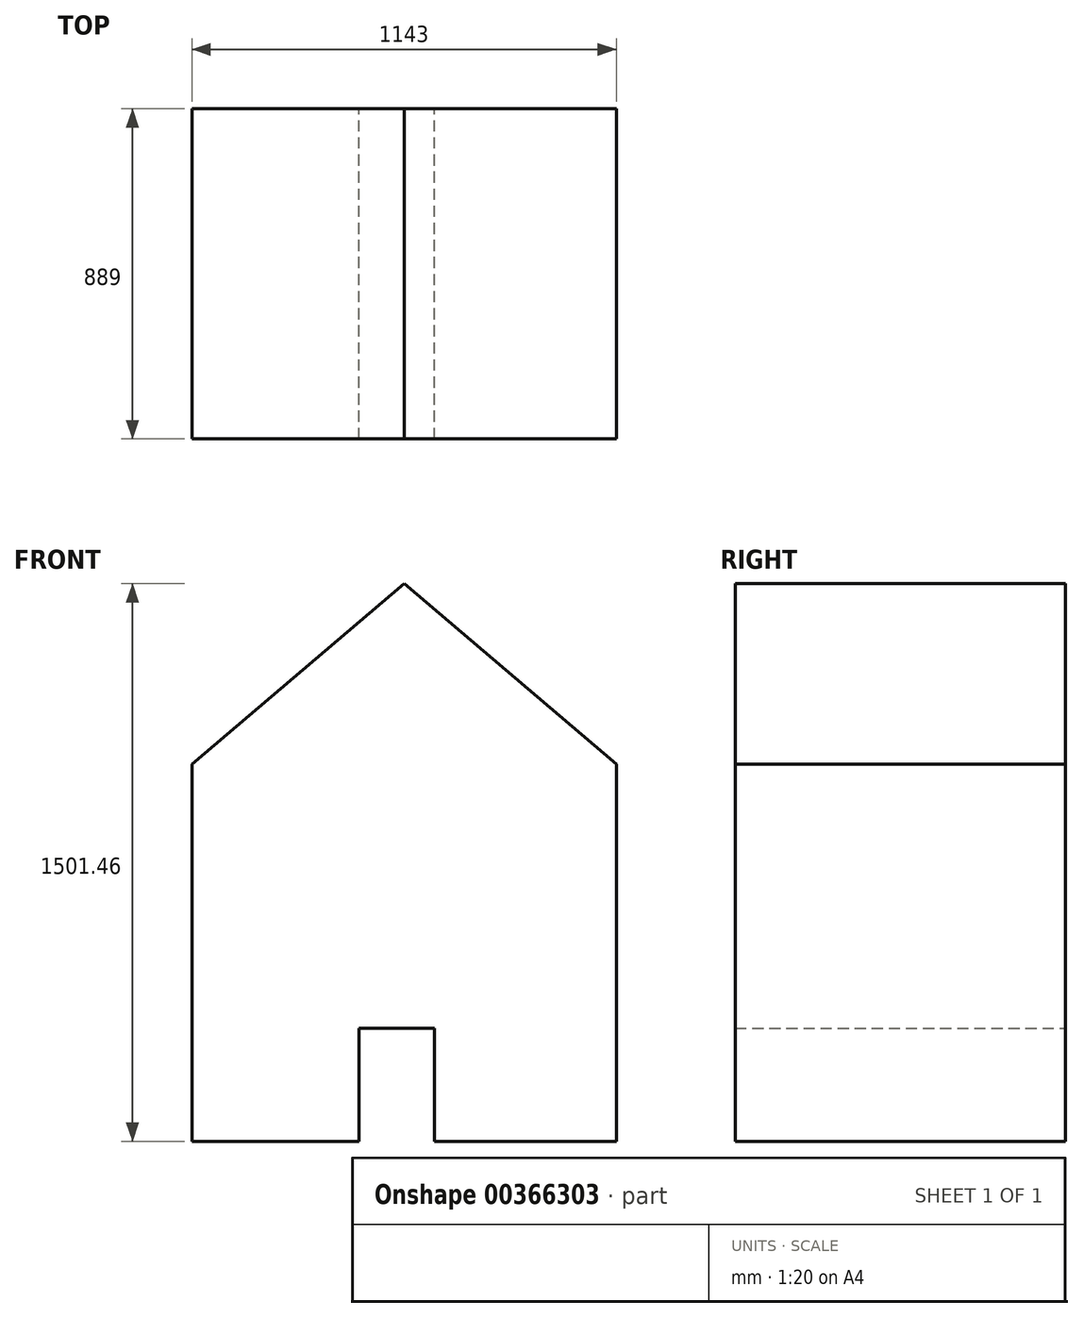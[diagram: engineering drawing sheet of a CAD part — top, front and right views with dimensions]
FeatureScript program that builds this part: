
annotation { "Feature Type Name" : "Feature", "Feature Type Description" : "" }
export const myFeature = defineFeature(function(context is Context, id is Id, definition is map)
    precondition{}
    {
        {
            var Q0;
            Q0=qCreatedBy(makeId("Front.planeOp"),FACE);
            var sketch = newSketch(context, id + "F0", { "sketchPlane" : qUnion([Q0])});
            skLineSegment(sketch, "E0", {"start": v(-85.93, -75) * mm, "end": v(1057.07, -75) * mm});
            skLineSegment(sketch, "E1", {"start": v(1057.07, -75) * mm, "end": v(1057.07, 941) * mm});
            skLineSegment(sketch, "E2", {"start": v(-85.93, -75) * mm, "end": v(-85.93, 941) * mm});
            skLineSegment(sketch, "E3", {"start": v(-85.93, 941) * mm, "end": v(485.57, 1426.45) * mm});
            skLineSegment(sketch, "E4", {"start": v(485.57, 1426.45) * mm, "end": v(1057.07, 941) * mm});
            skLineSegment(sketch, "E5", {"start": v(364.6, -75) * mm, "end": v(364.6, 229.8) * mm});
            skLineSegment(sketch, "E6", {"start": v(364.6, 229.8) * mm, "end": v(567.8, 229.8) * mm});
            skLineSegment(sketch, "E7", {"start": v(567.8, 229.8) * mm, "end": v(567.8, -75) * mm});
            skSolve(sketch);
        }
        {
            var Q0;
            {var subQ1=sQuery(id+"F0.wireOp",EDGE,"E1");Q0=makeQuery(id+"F0.imprint","IMPRINT",FACE,{"disambiguationData":[TD([[makeQuery(id+"F0.imprint","IMPRINT",EDGE,{"derivedFrom":subQ1}),1.0]])]});}
            extrude(context, id + "F1", {"entities" : qUnion([Q0]), "depth" : 889 * mm});
        }
    });
